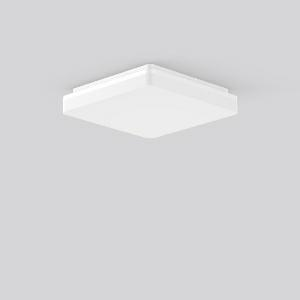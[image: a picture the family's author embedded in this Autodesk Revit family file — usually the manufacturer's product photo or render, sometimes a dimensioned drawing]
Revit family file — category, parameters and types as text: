
# Revit family: hb_506_221189_002_2_3973
name_source: partatom
category: Lighting Fixtures
units: mm (PartAtom-declared; Revit-internal decimal feet)

## family parameters
Cut with Voids When Loaded = No
Host = Face
Light Source = No
Part Type = Normal
Room Calculation Point = No
Round Connector Dimension = Use Diameter
Shared = No

## types (1)
- MultiColor 830 (1 x LED Modul 830, 1700 lm, 3000)
    Apparent Load = 18 VA
    CIE Flux Codes = 43 74 93 91 100
    Color Rendering = 80
    Color Temperature = 3000
    Default Elevation = 1800 mm
    Description = Series: HB 506
Ceiling and wall luminaire with slim design. Housing: plastic (polycarbonate). Diffuser: plastic (polycarbonate), opal. Base and diffuser are sealed together. MultiColour: Colour temperature adjustable via switching element. Choice of 3000 K or 4000 K. Factory setting is 3000 K. Quick mounting adapter galvanized steel sheet, with fastening screws. Driver integrated. 
Colour: white
Length: 260 mm
Width: 260 mm
Height: 53 mm
Lamp: LED
Socket: without socket
Colour temperature: 3000K, 4000K
Colour rendering index (CRI): 80
System power: 18 W
Rated luminous flux: 1700 lm
Luminous efficiency: 94 lm/W
System power 2: 18 W
Rated luminous flux 2: 1800 lm
Luminous efficiency 2: 100 lm/W
Control gear: EB
Protection class: I
Type of protection: IP 20
    Height = 53 mm
    Lamp = 1 x LED Modul 830
    Lamp Light Flux = 1700 lm
    Lamp count = 1
    Length = 260 mm
    Lifetime = 50000 h
    Luminous efficacy = 94 lm/W
    Manufacturer = RZB
    ModVariant = No
    Model = 221189.002.2
    Mounting Place = Ceiling, Wall
    Mounting Type = Surface mounted
    Number of Poles = 1
    OnlyDefault = Yes
    Power Factor = 1
    Product Name = HB 506
    Product group = Surface mounted ceiling and wall luminaires
    ProductGroupID = 305
    Protection Class = Protection class I
    Protection Degree = IP 20
    RLX_Detail_Level = 1
    RLX_Emergency_Light_Flux = 0 lm
    RLX_Emergency_Type = 0
    RLX_Emergency_Type_DB = No
    RlxData = <blob elided: 39325 chars, md5=6e557666>
    Socket = socket
    Standby Power = 0 W
    System Light Flux = 1700 lm
    System Power = 18 W
    Type Comments = MultiColor 830
    Type Image = 221189.002.jpg
    URL = http://relux.com
    VarID = multicolor_830
    Voltage = 230 V
    Voltage Range = 220-240 V
    Weight = 0.00 kg
    Width = 260 mm

## geometry (parser evidence)
native form markers: Blend x4, Sweep x14
no freeform markers — native parametric forms only
